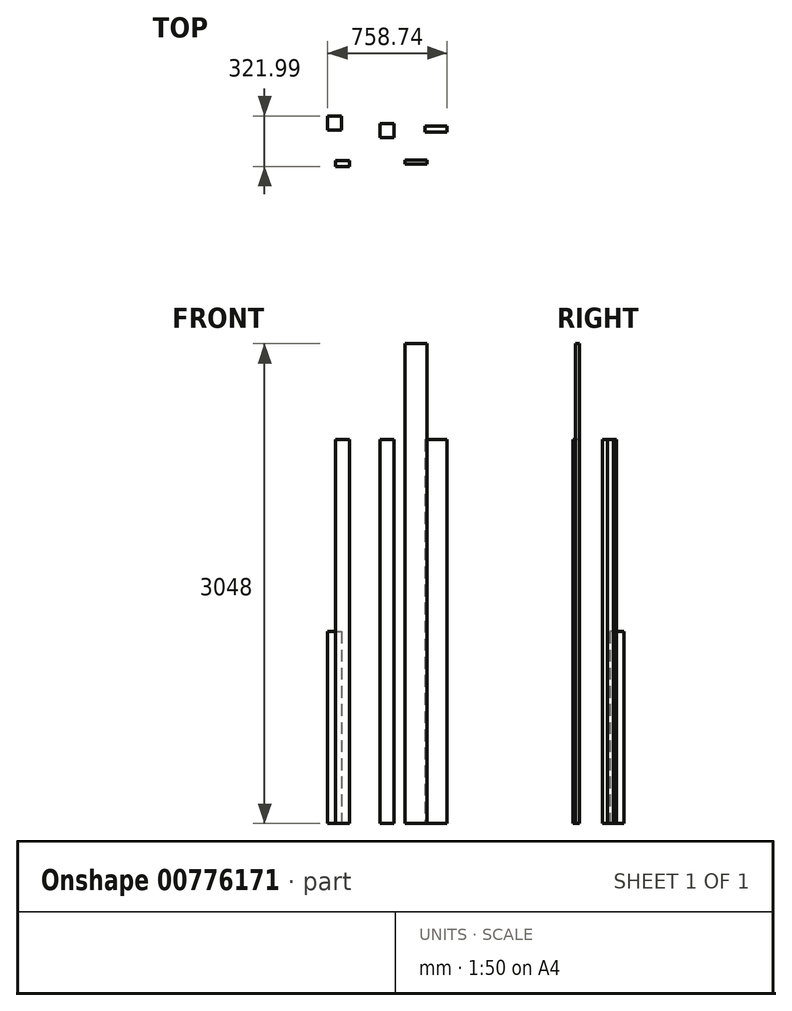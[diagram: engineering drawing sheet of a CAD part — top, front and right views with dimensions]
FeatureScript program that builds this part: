
annotation { "Feature Type Name" : "Feature", "Feature Type Description" : "" }
export const myFeature = defineFeature(function(context is Context, id is Id, definition is map)
    precondition{}
    {
        {
            var Q0;
            Q0=qCreatedBy(makeId("Top.planeOp"),FACE);
            var sketch = newSketch(context, id + "F0", { "sketchPlane" : qUnion([Q0])});
            skLineSegment(sketch, "E0.bottom", {"start": v(44.45, -44.45) * mm, "end": v(-44.45, -44.45) * mm});
            skLineSegment(sketch, "E0.top", {"start": v(44.45, 44.45) * mm, "end": v(-44.45, 44.45) * mm});
            skLineSegment(sketch, "E0.left", {"start": v(44.45, -44.45) * mm, "end": v(44.45, 44.45) * mm});
            skLineSegment(sketch, "E0.right", {"start": v(-44.45, -44.45) * mm, "end": v(-44.45, 44.45) * mm});
            skPoint(sketch, "E0.middle", {"position": v(0, 0) * mm});
            skSolve(sketch);
        }
        {
            var Q0;
            Q0=makeQuery(id+"F0.imprint","IMPRINT",FACE,{"disambiguationData":[TD([[makeQuery(id+"F0.imprint","IMPRINT",EDGE,{"derivedFrom":sQuery(id+"F0.wireOp",EDGE,"E0.bottom")}),-1.0]])]});
            extrude(context, id + "F1", {"entities" : qUnion([Q0]), "depth" : 2438.4 * mm, "offsetDistance" : 25.4 * mm});
        }
        {
            var Q0;
            Q0=qCreatedBy(makeId("Top.planeOp"),FACE);
            var sketch = newSketch(context, id + "F2", { "sketchPlane" : qUnion([Q0])});
            skLineSegment(sketch, "E1.bottom", {"start": v(-377.27, 91.9) * mm, "end": v(-288.37, 91.9) * mm});
            skLineSegment(sketch, "E1.top", {"start": v(-377.27, 3) * mm, "end": v(-288.37, 3) * mm});
            skLineSegment(sketch, "E1.left", {"start": v(-377.27, 91.9) * mm, "end": v(-377.27, 3) * mm});
            skLineSegment(sketch, "E1.right", {"start": v(-288.37, 91.9) * mm, "end": v(-288.37, 3) * mm});
            skLineSegment(sketch, "E2.bottom", {"start": v(241.77, 25.92) * mm, "end": v(381.47, 25.92) * mm});
            skLineSegment(sketch, "E2.top", {"start": v(241.77, -12.18) * mm, "end": v(381.47, -12.18) * mm});
            skLineSegment(sketch, "E2.left", {"start": v(241.77, 25.92) * mm, "end": v(241.77, -12.18) * mm});
            skLineSegment(sketch, "E2.right", {"start": v(381.47, 25.92) * mm, "end": v(381.47, -12.18) * mm});
            skLineSegment(sketch, "E3.bottom", {"start": v(-327.4, -192) * mm, "end": v(-238.5, -192) * mm});
            skLineSegment(sketch, "E3.top", {"start": v(-327.4, -230.1) * mm, "end": v(-238.5, -230.1) * mm});
            skLineSegment(sketch, "E3.left", {"start": v(-327.4, -192) * mm, "end": v(-327.4, -230.1) * mm});
            skLineSegment(sketch, "E3.right", {"start": v(-238.5, -192) * mm, "end": v(-238.5, -230.1) * mm});
            skLineSegment(sketch, "E4.bottom", {"start": v(113.84, -189.51) * mm, "end": v(253.54, -189.51) * mm});
            skLineSegment(sketch, "E4.top", {"start": v(113.84, -214.91) * mm, "end": v(253.54, -214.91) * mm});
            skLineSegment(sketch, "E4.left", {"start": v(113.84, -189.51) * mm, "end": v(113.84, -214.91) * mm});
            skLineSegment(sketch, "E4.right", {"start": v(253.54, -189.51) * mm, "end": v(253.54, -214.91) * mm});
            skSolve(sketch);
        }
        {
            var Q0;
            Q0=makeQuery(id+"F2.imprint","IMPRINT",FACE,{"disambiguationData":[TD([[makeQuery(id+"F2.imprint","IMPRINT",EDGE,{"derivedFrom":sQuery(id+"F2.wireOp",EDGE,"E1.bottom")}),-1.0]])]});
            extrude(context, id + "F3", {"entities" : qUnion([Q0]), "depth" : 1219.2 * mm, "offsetDistance" : 25.4 * mm});
        }
        {
            var Q0;
            Q0=makeQuery(id+"F2.imprint","IMPRINT",FACE,{"disambiguationData":[TD([[makeQuery(id+"F2.imprint","IMPRINT",EDGE,{"derivedFrom":sQuery(id+"F2.wireOp",EDGE,"E3.bottom")}),-1.0]])]});
            extrude(context, id + "F4", {"entities" : qUnion([Q0]), "depth" : 2438.4 * mm, "offsetDistance" : 25.4 * mm});
        }
        {
            var Q0;
            Q0=makeQuery(id+"F2.imprint","IMPRINT",FACE,{"disambiguationData":[TD([[makeQuery(id+"F2.imprint","IMPRINT",EDGE,{"derivedFrom":sQuery(id+"F2.wireOp",EDGE,"E4.bottom")}),-1.0]])]});
            extrude(context, id + "F5", {"entities" : qUnion([Q0]), "depth" : 3048 * mm, "offsetDistance" : 25.4 * mm});
        }
        {
            var Q0;
            Q0=makeQuery(id+"F2.imprint","IMPRINT",FACE,{"disambiguationData":[TD([[makeQuery(id+"F2.imprint","IMPRINT",EDGE,{"derivedFrom":sQuery(id+"F2.wireOp",EDGE,"E2.bottom")}),-1.0]])]});
            extrude(context, id + "F6", {"entities" : qUnion([Q0]), "depth" : 2438.4 * mm, "offsetDistance" : 25.4 * mm});
        }
    });
